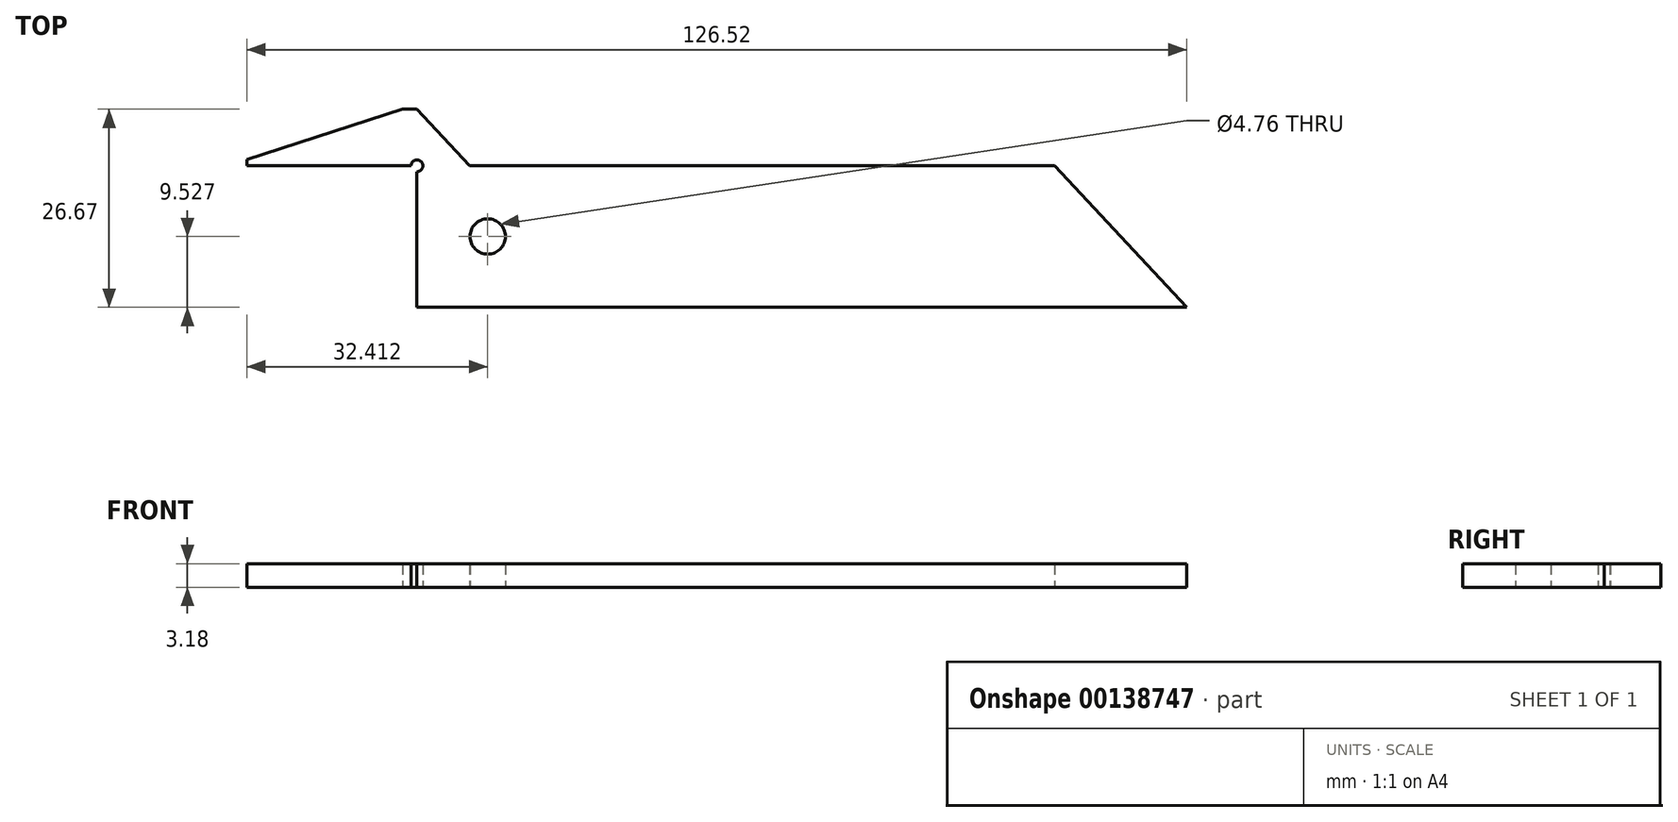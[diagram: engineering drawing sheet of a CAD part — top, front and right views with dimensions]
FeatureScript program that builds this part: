
annotation { "Feature Type Name" : "Feature", "Feature Type Description" : "" }
export const myFeature = defineFeature(function(context is Context, id is Id, definition is map)
    precondition{}
    {
        {
            var Q0;
            Q0=qCreatedBy(makeId("Top.planeOp"),FACE);
            var sketch = newSketch(context, id + "F0", { "sketchPlane" : qUnion([Q0])});
            skLineSegment(sketch, "E0", {"start": v(-25.4, -33.04) * mm, "end": v(78.24, -33.04) * mm});
            skLineSegment(sketch, "E1", {"start": v(78.24, -33.04) * mm, "end": v(60.46, -13.99) * mm});
            skLineSegment(sketch, "E2", {"start": v(60.46, -13.99) * mm, "end": v(-18.28, -13.99) * mm});
            skLineSegment(sketch, "E3", {"start": v(-18.28, -13.99) * mm, "end": v(-25.4, -6.37) * mm});
            skLineSegment(sketch, "E4", {"start": v(-25.4, -6.37) * mm, "end": v(-27.35, -6.37) * mm});
            skLineSegment(sketch, "E5", {"start": v(-48.28, -13.17) * mm, "end": v(-48.28, -13.99) * mm});
            skLineSegment(sketch, "E6", {"start": v(-48.28, -13.99) * mm, "end": v(-26.19, -13.99) * mm});
            skLineSegment(sketch, "E7", {"start": v(-25.4, -14.78) * mm, "end": v(-25.4, -33.04) * mm});
            skLineSegment(sketch, "E8", {"start": v(-25.4, -6.37) * mm, "end": v(-25.4, -13.99) * mm, "construction": true});
            skLineSegment(sketch, "E9", {"start": v(-48.28, -13.17) * mm, "end": v(-27.35, -6.37) * mm});
            skArc(sketch, "E10", {"start": v(-25.4, -14.78) * mm, "mid": v(-24.83, -13.43) * mm, "end": v(-26.19, -13.99) * mm});
            skCircle(sketch, "E11", {"center": v(-15.87, -23.51) * mm, "radius": 2.38 * mm});
            skSolve(sketch);
        }
        {
            var Q0;
            Q0=makeQuery(id+"F0.imprint","IMPRINT",FACE,{"disambiguationData":[TD([[makeQuery(id+"F0.imprint","IMPRINT",EDGE,{"derivedFrom":sQuery(id+"F0.wireOp",EDGE,"E0")}),1.0]])]});
            extrude(context, id + "F1", {"entities" : qUnion([Q0]), "depth" : 3.17 * mm});
        }
    });
